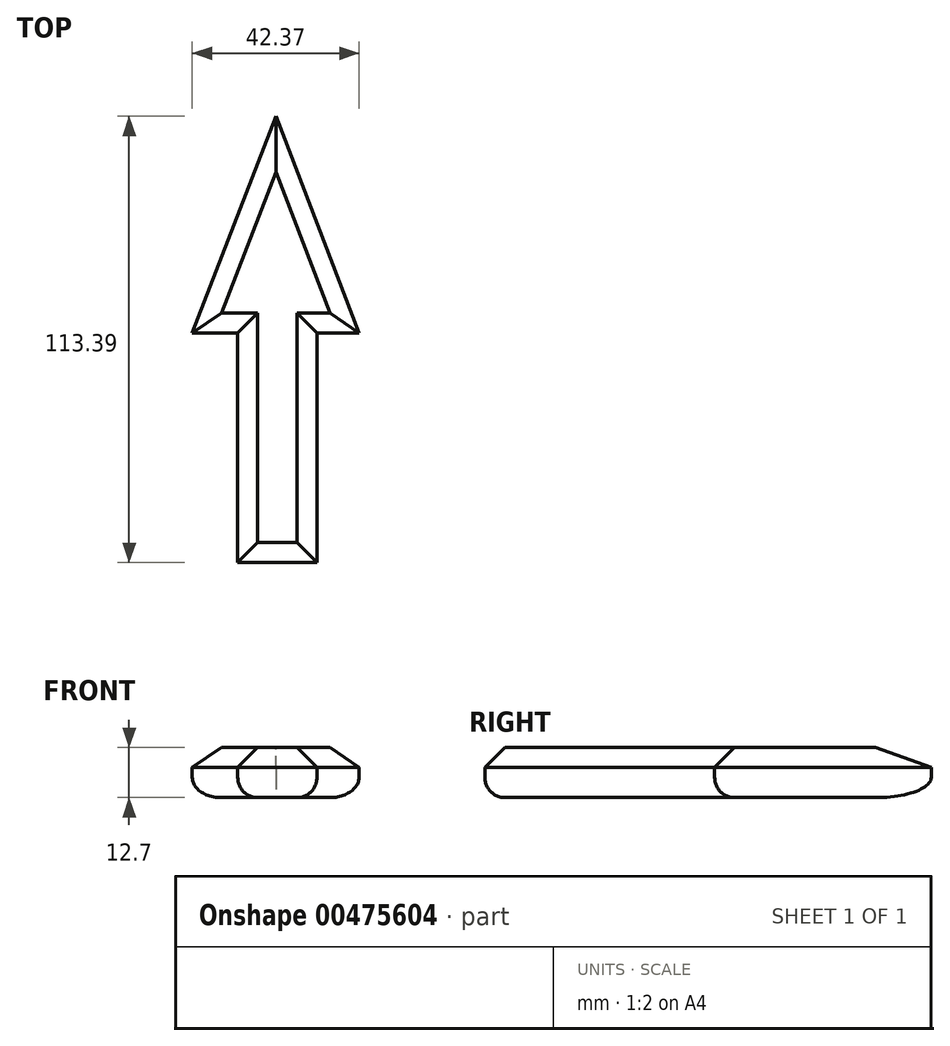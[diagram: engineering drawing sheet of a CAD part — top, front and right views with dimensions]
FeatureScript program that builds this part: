
annotation { "Feature Type Name" : "Feature", "Feature Type Description" : "" }
export const myFeature = defineFeature(function(context is Context, id is Id, definition is map)
    precondition{}
    {
        {
            var Q0;
            Q0=qCreatedBy(makeId("Top.planeOp"),FACE);
            var sketch = newSketch(context, id + "F0", { "sketchPlane" : qUnion([Q0])});
            skLineSegment(sketch, "E0", {"start": v(0, 55.02) * mm, "end": v(-21.34, 0) * mm});
            skLineSegment(sketch, "E1", {"start": v(0, 55.02) * mm, "end": v(21.03, 0) * mm});
            skLineSegment(sketch, "E2", {"start": v(21.03, 0) * mm, "end": v(-21.34, 0) * mm});
            skLineSegment(sketch, "E3", {"start": v(-9.75, 0) * mm, "end": v(-9.75, -58.37) * mm});
            skLineSegment(sketch, "E4", {"start": v(-9.75, -58.37) * mm, "end": v(10.36, -58.37) * mm});
            skLineSegment(sketch, "E5", {"start": v(10.36, -58.37) * mm, "end": v(10.36, 0) * mm});
            skSolve(sketch);
        }
        {
            var Q0;
            Q0 = qSketchRegion(id + "F0", true);
            extrude(context, id + "F1", {"entities" : qUnion([Q0]), "depth" : 12.7 * mm});
        }
        {
            var Q0;
            Q0=makeQuery(id+"F1.opExtrude","CAP_FACE",FACE,{"disambiguationData":[OSD([sQuery(id+"F0.wireOp",EDGE,"E0"),sQuery(id+"F0.wireOp",EDGE,"E1"),sQuery(id+"F0.wireOp",EDGE,"E2"),sQuery(id+"F0.wireOp",EDGE,"E3"),sQuery(id+"F0.wireOp",EDGE,"E4"),sQuery(id+"F0.wireOp",EDGE,"E5")])],"isStart":false});
            chamfer(context, id + "F2", {"entities" : qUnion([Q0]), "width" : 5.08 * mm, "tangentPropagation" : true});
        }
        {
            var Q0;
            Q0=makeQuery(id+"F1.opExtrude","CAP_FACE",FACE,{"disambiguationData":[OSD([sQuery(id+"F0.wireOp",EDGE,"E0"),sQuery(id+"F0.wireOp",EDGE,"E1"),sQuery(id+"F0.wireOp",EDGE,"E2"),sQuery(id+"F0.wireOp",EDGE,"E3"),sQuery(id+"F0.wireOp",EDGE,"E4"),sQuery(id+"F0.wireOp",EDGE,"E5")])],"isStart":true});
            fillet(context, id + "F3", {"entities" : qUnion([Q0]), "radius" : 5.08 * mm, "tangentPropagation" : true, "allowEdgeOverflow" : false});
        }
    });
